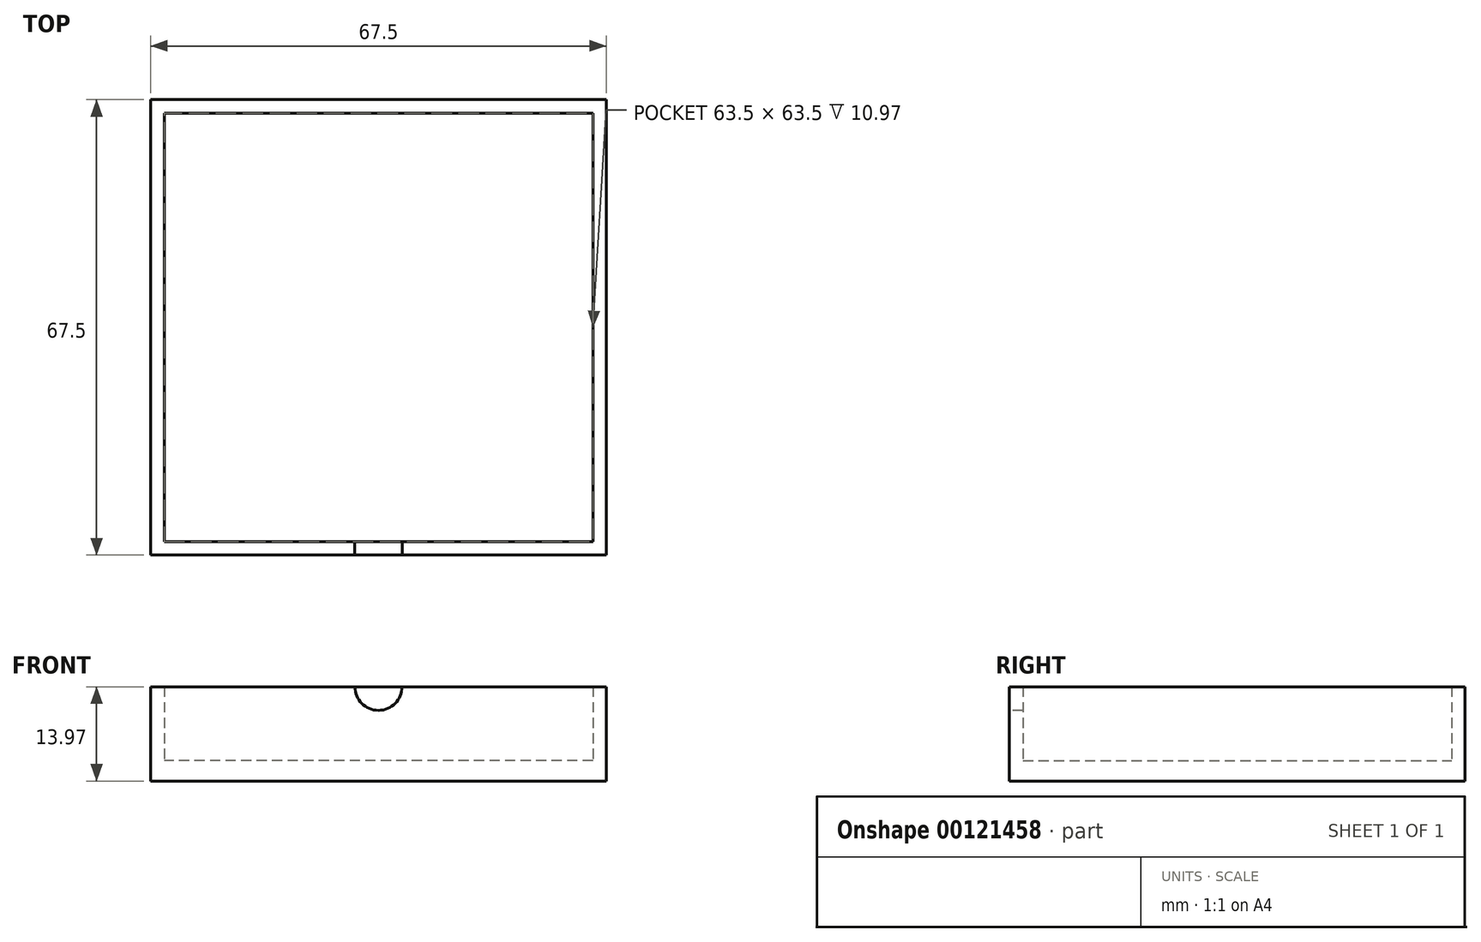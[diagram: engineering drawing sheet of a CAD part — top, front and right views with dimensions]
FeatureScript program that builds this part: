
annotation { "Feature Type Name" : "Feature", "Feature Type Description" : "" }
export const myFeature = defineFeature(function(context is Context, id is Id, definition is map)
    precondition{}
    {
        {
            var Q0;
            Q0=qCreatedBy(makeId("Top.planeOp"),FACE);
            var sketch = newSketch(context, id + "F0", { "sketchPlane" : qUnion([Q0])});
            skLineSegment(sketch, "E0.bottom", {"start": v(-31.75, 31.75) * mm, "end": v(31.75, 31.75) * mm});
            skLineSegment(sketch, "E0.top", {"start": v(-31.75, -31.75) * mm, "end": v(31.75, -31.75) * mm});
            skLineSegment(sketch, "E0.left", {"start": v(-31.75, 31.75) * mm, "end": v(-31.75, -31.75) * mm});
            skLineSegment(sketch, "E0.right", {"start": v(31.75, 31.75) * mm, "end": v(31.75, -31.75) * mm});
            skLineSegment(sketch, "E1", {"start": v(0, 31.75) * mm, "end": v(0, -31.75) * mm, "construction": true});
            skLineSegment(sketch, "E2.0", {"start": v(-33.75, 33.75) * mm, "end": v(-33.75, -33.75) * mm});
            skLineSegment(sketch, "E2.1", {"start": v(-33.75, 33.75) * mm, "end": v(33.75, 33.75) * mm});
            skLineSegment(sketch, "E2.2", {"start": v(33.75, 33.75) * mm, "end": v(33.75, -33.75) * mm});
            skLineSegment(sketch, "E2.3", {"start": v(-33.75, -33.75) * mm, "end": v(33.75, -33.75) * mm});
            skLineSegment(sketch, "E3.0", {"start": v(-34.75, 34.75) * mm, "end": v(-34.75, -34.75) * mm, "construction": true});
            skLineSegment(sketch, "E3.1", {"start": v(-34.75, 34.75) * mm, "end": v(34.75, 34.75) * mm, "construction": true});
            skLineSegment(sketch, "E3.2", {"start": v(34.75, 34.75) * mm, "end": v(34.75, -34.75) * mm, "construction": true});
            skLineSegment(sketch, "E3.3", {"start": v(-34.75, -34.75) * mm, "end": v(34.75, -34.75) * mm, "construction": true});
            skCircle(sketch, "E4", {"center": v(0, 0) * mm, "radius": 3.5 * mm});
            skSolve(sketch);
        }
        {
            var Q0;
            Q0=makeQuery(id+"F0.imprint","IMPRINT",FACE,{"disambiguationData":[TD([[makeQuery(id+"F0.imprint","IMPRINT",EDGE,{"derivedFrom":sQuery(id+"F0.wireOp",EDGE,"E0.bottom")}),1.0]])]});
            var Q1;
            Q1=makeQuery(id+"F0.imprint","IMPRINT",FACE,{"disambiguationData":[TD([[makeQuery(id+"F0.imprint","IMPRINT",EDGE,{"derivedFrom":sQuery(id+"F0.wireOp",EDGE,"E0.bottom")}),-1.0]])]});
            extrude(context, id + "F1", {"entities" : qUnion([Q0, Q1]), "depth" : 3 * mm});
        }
        {
            var Q0;
            Q0=makeQuery(id+"F0.imprint","IMPRINT",FACE,{"disambiguationData":[TD([[makeQuery(id+"F0.imprint","IMPRINT",EDGE,{"derivedFrom":sQuery(id+"F0.wireOp",EDGE,"E0.bottom")}),1.0]])]});
            extrude(context, id + "F2", {"entities" : qUnion([Q0]), "operationType" : NewBodyOperationType.ADD, "depth" : 13.97 * mm});
        }
        {
            var Q0;
            {var subQ0=sQuery(id+"F0.wireOp",EDGE,"E2.3");Q0=makeQuery(id+"F2.boolean.opBoolean","MERGE",FACE,{"derivedFrom":[makeQuery(id+"F1.opExtrude","SWEPT_FACE",FACE,{"disambiguationData":[OSD([subQ0])]}),makeQuery(id+"F2.opExtrude","SWEPT_FACE",FACE,{"disambiguationData":[OSD([subQ0])]})]});}
            var sketch = newSketch(context, id + "F3", { "sketchPlane" : qUnion([Q0])});
            skCircle(sketch, "E5", {"center": v(0, 13.97) * mm, "radius": 3.5 * mm});
            skSolve(sketch);
        }
        {
            var Q0;
            {var subQ0=sQuery(id+"F3.wireOp",EDGE,"E5");var subQ1=makeQuery(id+"F2.opExtrude","CAP_EDGE",EDGE,{"disambiguationData":[OSD([sQuery(id+"F0.wireOp",EDGE,"E2.3")])],"isStart":false});var subQ2=makeQuery(id+"F3.imprint","INTERSECT",VERTEX,{"disambiguationData":[OD(0.0)],"derivedFrom":[subQ1,subQ0]});Q0=makeQuery(id+"F3.imprint","IMPRINT",FACE,{"disambiguationData":[TD([[makeQuery(id+"F3.imprint","IMPRINT",EDGE,{"disambiguationData":[TD([[subQ2,-1.0]])],"derivedFrom":subQ0}),1.0]])]});}
            var Q1;
            {var subQ0=sQuery(id+"F3.wireOp",EDGE,"E5");var subQ1=makeQuery(id+"F2.opExtrude","CAP_EDGE",EDGE,{"disambiguationData":[OSD([sQuery(id+"F0.wireOp",EDGE,"E2.3")])],"isStart":false});var subQ2=makeQuery(id+"F3.imprint","INTERSECT",VERTEX,{"disambiguationData":[OD(0.0)],"derivedFrom":[subQ1,subQ0]});Q1=makeQuery(id+"F3.imprint","IMPRINT",FACE,{"disambiguationData":[TD([[makeQuery(id+"F3.imprint","IMPRINT",EDGE,{"disambiguationData":[TD([[subQ2,1.0]])],"derivedFrom":subQ0}),1.0]])]});}
            var Q2;
            Q2=makeQuery(id+"F2.opExtrude","SWEPT_FACE",FACE,{"disambiguationData":[OSD([sQuery(id+"F0.wireOp",EDGE,"E0.top")])]});
            extrude(context, id + "F4", {"entities" : qUnion([Q0, Q1]), "operationType" : NewBodyOperationType.REMOVE, "endBound" : BoundingType.UP_TO_SURFACE, "oppositeDirection" : true, "endBoundEntityFace" : qUnion([Q2]), "depth" : 25 * mm});
        }
        {
            var Q0;
            Q0=makeQuery(id+"F0.imprint","IMPRINT",FACE,{"disambiguationData":[TD([[makeQuery(id+"F0.imprint","IMPRINT",EDGE,{"derivedFrom":sQuery(id+"F0.wireOp",EDGE,"E0.bottom")}),-1.0]])]});
            var Q1;
            Q1=makeQuery(id+"F0.imprint","IMPRINT",FACE,{"disambiguationData":[TD([[makeQuery(id+"F0.imprint","IMPRINT",EDGE,{"derivedFrom":sQuery(id+"F0.wireOp",EDGE,"E4")}),1.0]])]});
            var Q2;
            Q2=makeQuery(id+"F0.imprint","IMPRINT",FACE,{"disambiguationData":[TD([[makeQuery(id+"F0.imprint","IMPRINT",EDGE,{"derivedFrom":sQuery(id+"F0.wireOp",EDGE,"E0.bottom")}),1.0]])]});
            extrude(context, id + "F5", {"entities" : qUnion([Q0, Q1, Q2]), "depth" : 2 * mm});
        }
        {
            var Q0;
            Q0=makeQuery(id+"F0.imprint","IMPRINT",FACE,{"disambiguationData":[TD([[makeQuery(id+"F0.imprint","IMPRINT",EDGE,{"derivedFrom":sQuery(id+"F0.wireOp",EDGE,"E0.bottom")}),-1.0]])]});
            var Q1;
            Q1=makeQuery(id+"F0.imprint","IMPRINT",FACE,{"disambiguationData":[TD([[makeQuery(id+"F0.imprint","IMPRINT",EDGE,{"derivedFrom":sQuery(id+"F0.wireOp",EDGE,"E4")}),1.0]])]});
            extrude(context, id + "F6", {"entities" : qUnion([Q0, Q1]), "operationType" : NewBodyOperationType.ADD, "depth" : 3 * mm});
        }
    });
